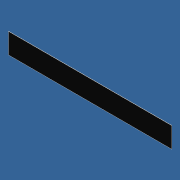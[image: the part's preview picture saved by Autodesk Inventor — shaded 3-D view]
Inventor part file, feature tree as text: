
AUTODESK INVENTOR PART (.ipt)
format: ipt  version: 2012 (Build 160160000, 160)  size: 63,488 bytes
history: native  units: in
note: dims shown in document units (in); Inventor stores cm internally (conversion verified against a paired STEP export)
features: extrude x1, sketch x1
ambient origin geometry x8: Origin, YZ Plane, XZ Plane, XY Plane, X Axis, Y Axis, Z Axis, Center Point
bodies: Solid1 (feature_tree)
feature tree (2):
  extrude  "Extrusion1"  Depth=2.0in
  sketch  "Sketch1"  dims[d0=16.0in d1=2.0in d2=0.025in d3=0.0in]
